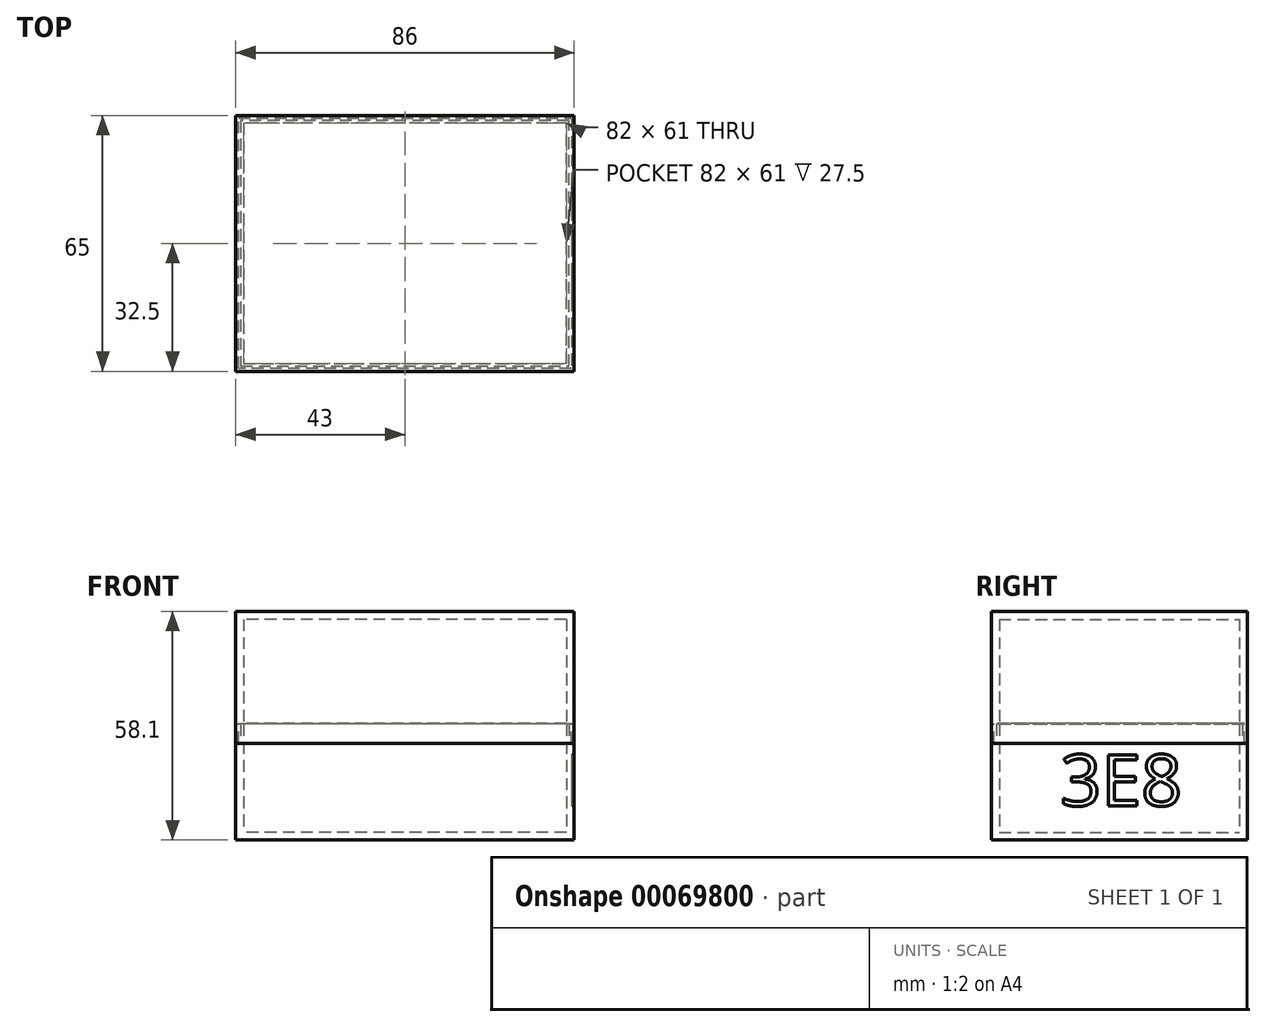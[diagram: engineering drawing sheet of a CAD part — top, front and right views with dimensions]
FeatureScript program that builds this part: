
annotation { "Feature Type Name" : "Feature", "Feature Type Description" : "" }
export const myFeature = defineFeature(function(context is Context, id is Id, definition is map)
    precondition{}
    {
        {
            var Q0;
            Q0=qCreatedBy(makeId("Top.planeOp"),FACE);
            var sketch = newSketch(context, id + "F0", { "sketchPlane" : qUnion([Q0])});
            skLineSegment(sketch, "E0.rect.bottom", {"start": v(43, -32.5) * mm, "end": v(-43, -32.5) * mm});
            skLineSegment(sketch, "E0.rect.top", {"start": v(43, 32.5) * mm, "end": v(-43, 32.5) * mm});
            skLineSegment(sketch, "E0.rect.left", {"start": v(43, -32.5) * mm, "end": v(43, 32.5) * mm});
            skLineSegment(sketch, "E0.rect.right", {"start": v(-43, -32.5) * mm, "end": v(-43, 32.5) * mm});
            skPoint(sketch, "E0.rect.middle", {"position": v(0, 0) * mm});
            skSolve(sketch);
        }
        {
            var Q0;
            Q0 = qSketchRegion(id + "F0", true);
            extrude(context, id + "F1", {"entities" : qUnion([Q0]), "depth" : 2 * mm});
        }
        {
            var Q0;
            Q0=makeQuery(id+"F1.opExtrude","CAP_FACE",FACE,{"disambiguationData":[OSD([sQuery(id+"F0.wireOp",EDGE,"E0.rect.bottom"),sQuery(id+"F0.wireOp",EDGE,"E0.rect.top"),sQuery(id+"F0.wireOp",EDGE,"E0.rect.left"),sQuery(id+"F0.wireOp",EDGE,"E0.rect.right")])],"isStart":false});
            var sketch = newSketch(context, id + "F2", { "sketchPlane" : qUnion([Q0])});
            skLineSegment(sketch, "E1.0.0", {"start": v(-43, -32.5) * mm, "end": v(43, -32.5) * mm});
            skLineSegment(sketch, "E1.0.1", {"start": v(43, -32.5) * mm, "end": v(43, 32.5) * mm});
            skLineSegment(sketch, "E1.0.2", {"start": v(43, 32.5) * mm, "end": v(-43, 32.5) * mm});
            skLineSegment(sketch, "E1.0.3", {"start": v(-43, 32.5) * mm, "end": v(-43, -32.5) * mm});
            skLineSegment(sketch, "E2.0", {"start": v(41, 30.5) * mm, "end": v(-41, 30.5) * mm});
            skLineSegment(sketch, "E2.1", {"start": v(41, -30.5) * mm, "end": v(41, 30.5) * mm});
            skLineSegment(sketch, "E2.2", {"start": v(-41, -30.5) * mm, "end": v(41, -30.5) * mm});
            skLineSegment(sketch, "E2.3", {"start": v(-41, 30.5) * mm, "end": v(-41, -30.5) * mm});
            skSolve(sketch);
        }
        {
            var Q0;
            Q0 = qSketchRegion(id + "F2", true);
            extrude(context, id + "F3", {"entities" : qUnion([Q0]), "operationType" : NewBodyOperationType.ADD, "depth" : 22.5 * mm});
        }
        {
            var Q0;
            Q0=makeQuery(id+"F3.opExtrude","CAP_FACE",FACE,{"disambiguationData":[OSD([sQuery(id+"F2.wireOp",EDGE,"E1.0.0"),sQuery(id+"F2.wireOp",EDGE,"E1.0.1"),sQuery(id+"F2.wireOp",EDGE,"E1.0.2"),sQuery(id+"F2.wireOp",EDGE,"E1.0.3"),sQuery(id+"F2.wireOp",EDGE,"E2.0"),sQuery(id+"F2.wireOp",EDGE,"E2.1"),sQuery(id+"F2.wireOp",EDGE,"E2.2"),sQuery(id+"F2.wireOp",EDGE,"E2.3")])],"isStart":false});
            var sketch = newSketch(context, id + "F4", { "sketchPlane" : qUnion([Q0])});
            skLineSegment(sketch, "E3.0", {"start": v(-41, 30.5) * mm, "end": v(-41, -30.5) * mm});
            skLineSegment(sketch, "E4.0", {"start": v(41, 30.5) * mm, "end": v(-41, 30.5) * mm});
            skLineSegment(sketch, "E5.0", {"start": v(-41, -30.5) * mm, "end": v(41, -30.5) * mm});
            skLineSegment(sketch, "E6.0", {"start": v(41, -30.5) * mm, "end": v(41, 30.5) * mm});
            skLineSegment(sketch, "E7.0", {"start": v(41.7, 31.2) * mm, "end": v(-41.7, 31.2) * mm});
            skLineSegment(sketch, "E7.1", {"start": v(41.7, -31.2) * mm, "end": v(41.7, 31.2) * mm});
            skLineSegment(sketch, "E7.2", {"start": v(-41.7, -31.2) * mm, "end": v(41.7, -31.2) * mm});
            skLineSegment(sketch, "E7.3", {"start": v(-41.7, 31.2) * mm, "end": v(-41.7, -31.2) * mm});
            skSolve(sketch);
        }
        {
            var Q0;
            Q0 = qSketchRegion(id + "F4", true);
            extrude(context, id + "F5", {"entities" : qUnion([Q0]), "operationType" : NewBodyOperationType.ADD, "depth" : 5 * mm});
        }
        {
            var Q0;
            Q0=makeQuery(id+"F5.opExtrude","CAP_FACE",FACE,{"disambiguationData":[OSD([sQuery(id+"F4.wireOp",EDGE,"E3.0"),sQuery(id+"F4.wireOp",EDGE,"E4.0"),sQuery(id+"F4.wireOp",EDGE,"E5.0"),sQuery(id+"F4.wireOp",EDGE,"E6.0"),sQuery(id+"F4.wireOp",EDGE,"E7.0"),sQuery(id+"F4.wireOp",EDGE,"E7.1"),sQuery(id+"F4.wireOp",EDGE,"E7.2"),sQuery(id+"F4.wireOp",EDGE,"E7.3")])],"isStart":false});
            cPlane(context, id + "F6", {"entities" : qUnion([Q0]), "cplaneType" : CPlaneType.OFFSET, "offset" : .1 * mm, "width" : 150 * mm, "height" : 150 * mm});
        }
        {
            var Q0;
            Q0=qCreatedBy(id+"F6.planeOp",FACE);
            var sketch = newSketch(context, id + "F7", { "sketchPlane" : qUnion([Q0])});
            skLineSegment(sketch, "E8.0.0", {"start": v(43, -32.5) * mm, "end": v(-43, -32.5) * mm});
            skLineSegment(sketch, "E8.0.1", {"start": v(-43, -32.5) * mm, "end": v(-43, 32.5) * mm});
            skLineSegment(sketch, "E8.0.2", {"start": v(-43, 32.5) * mm, "end": v(43, 32.5) * mm});
            skLineSegment(sketch, "E8.0.3", {"start": v(43, 32.5) * mm, "end": v(43, -32.5) * mm});
            skSolve(sketch);
        }
        {
            var Q0;
            Q0 = qSketchRegion(id + "F7", true);
            extrude(context, id + "F8", {"entities" : qUnion([Q0]), "depth" : 28.5 * mm});
        }
        {
            var Q0;
            Q0=makeQuery(id+"F8.opExtrude","CAP_FACE",FACE,{"disambiguationData":[OSD([sQuery(id+"F7.wireOp",EDGE,"E8.0.0"),sQuery(id+"F7.wireOp",EDGE,"E8.0.1"),sQuery(id+"F7.wireOp",EDGE,"E8.0.2"),sQuery(id+"F7.wireOp",EDGE,"E8.0.3")])],"isStart":true});
            var sketch = newSketch(context, id + "F9", { "sketchPlane" : qUnion([Q0])});
            skLineSegment(sketch, "E9.0.0", {"start": v(41, -30.5) * mm, "end": v(-41, -30.5) * mm});
            skLineSegment(sketch, "E9.0.1", {"start": v(-41, -30.5) * mm, "end": v(-41, 30.5) * mm});
            skLineSegment(sketch, "E9.0.2", {"start": v(-41, 30.5) * mm, "end": v(41, 30.5) * mm});
            skLineSegment(sketch, "E9.0.3", {"start": v(41, 30.5) * mm, "end": v(41, -30.5) * mm});
            skSolve(sketch);
        }
        {
            var Q0;
            Q0 = qSketchRegion(id + "F9", true);
            extrude(context, id + "F10", {"entities" : qUnion([Q0]), "operationType" : NewBodyOperationType.REMOVE, "oppositeDirection" : true, "depth" : 26.5 * mm});
        }
        {
            var Q0;
            Q0=makeQuery(id+"F8.opExtrude","CAP_FACE",FACE,{"disambiguationData":[OSD([sQuery(id+"F7.wireOp",EDGE,"E8.0.0"),sQuery(id+"F7.wireOp",EDGE,"E8.0.1"),sQuery(id+"F7.wireOp",EDGE,"E8.0.2"),sQuery(id+"F7.wireOp",EDGE,"E8.0.3")])],"isStart":true});
            var sketch = newSketch(context, id + "F11", { "sketchPlane" : qUnion([Q0])});
            skLineSegment(sketch, "E10.0", {"start": v(43, -32.5) * mm, "end": v(43, 32.5) * mm});
            skLineSegment(sketch, "E11.0", {"start": v(43, 32.5) * mm, "end": v(-43, 32.5) * mm});
            skLineSegment(sketch, "E12.0", {"start": v(-43, 32.5) * mm, "end": v(-43, -32.5) * mm});
            skLineSegment(sketch, "E13.0", {"start": v(-43, -32.5) * mm, "end": v(43, -32.5) * mm});
            skLineSegment(sketch, "E14.0", {"start": v(42.3, -31.8) * mm, "end": v(42.3, 31.8) * mm});
            skLineSegment(sketch, "E14.1", {"start": v(-42.3, -31.8) * mm, "end": v(42.3, -31.8) * mm});
            skLineSegment(sketch, "E14.2", {"start": v(-42.3, 31.8) * mm, "end": v(-42.3, -31.8) * mm});
            skLineSegment(sketch, "E14.3", {"start": v(42.3, 31.8) * mm, "end": v(-42.3, 31.8) * mm});
            skSolve(sketch);
        }
        {
            var Q0;
            Q0 = qSketchRegion(id + "F11", true);
            extrude(context, id + "F12", {"entities" : qUnion([Q0]), "operationType" : NewBodyOperationType.ADD, "depth" : 5 * mm});
        }
        {
            var Q0;
            Q0=makeQuery(id+"F3.boolean.opBoolean","MERGE",FACE,{"derivedFrom":[makeQuery(id+"F1.opExtrude","SWEPT_FACE",FACE,{"disambiguationData":[OSD([sQuery(id+"F0.wireOp",EDGE,"E0.rect.left")])]}),makeQuery(id+"F3.opExtrude","SWEPT_FACE",FACE,{"disambiguationData":[OSD([sQuery(id+"F2.wireOp",EDGE,"E1.0.1")])]})]});
            var sketch = newSketch(context, id + "F13", { "sketchPlane" : qUnion([Q0])});
            skText(sketch, "E15", { "text": "3E8", "fontName": "OpenSans-Regular.ttf"});
            skLineSegment(sketch, "E16", {"start": v(32.5, 24.5) * mm, "end": v(-32.5, 0) * mm, "construction": true});
            skPoint(sketch, "E17", {"position": v(0, 12.25) * mm});
            const initialGuessF13  = {"E15": [-0.015, 0.0087, 1, 0, 0.0131]};
            skSetInitialGuess(sketch, initialGuessF13);
            skSolve(sketch);
        }
        {
            var Q0;
            Q0 = qSketchRegion(id + "F13", true);
            extrude(context, id + "F14", {"entities" : qUnion([Q0]), "operationType" : NewBodyOperationType.REMOVE, "oppositeDirection" : true, "depth" : .5 * mm});
        }
    });
